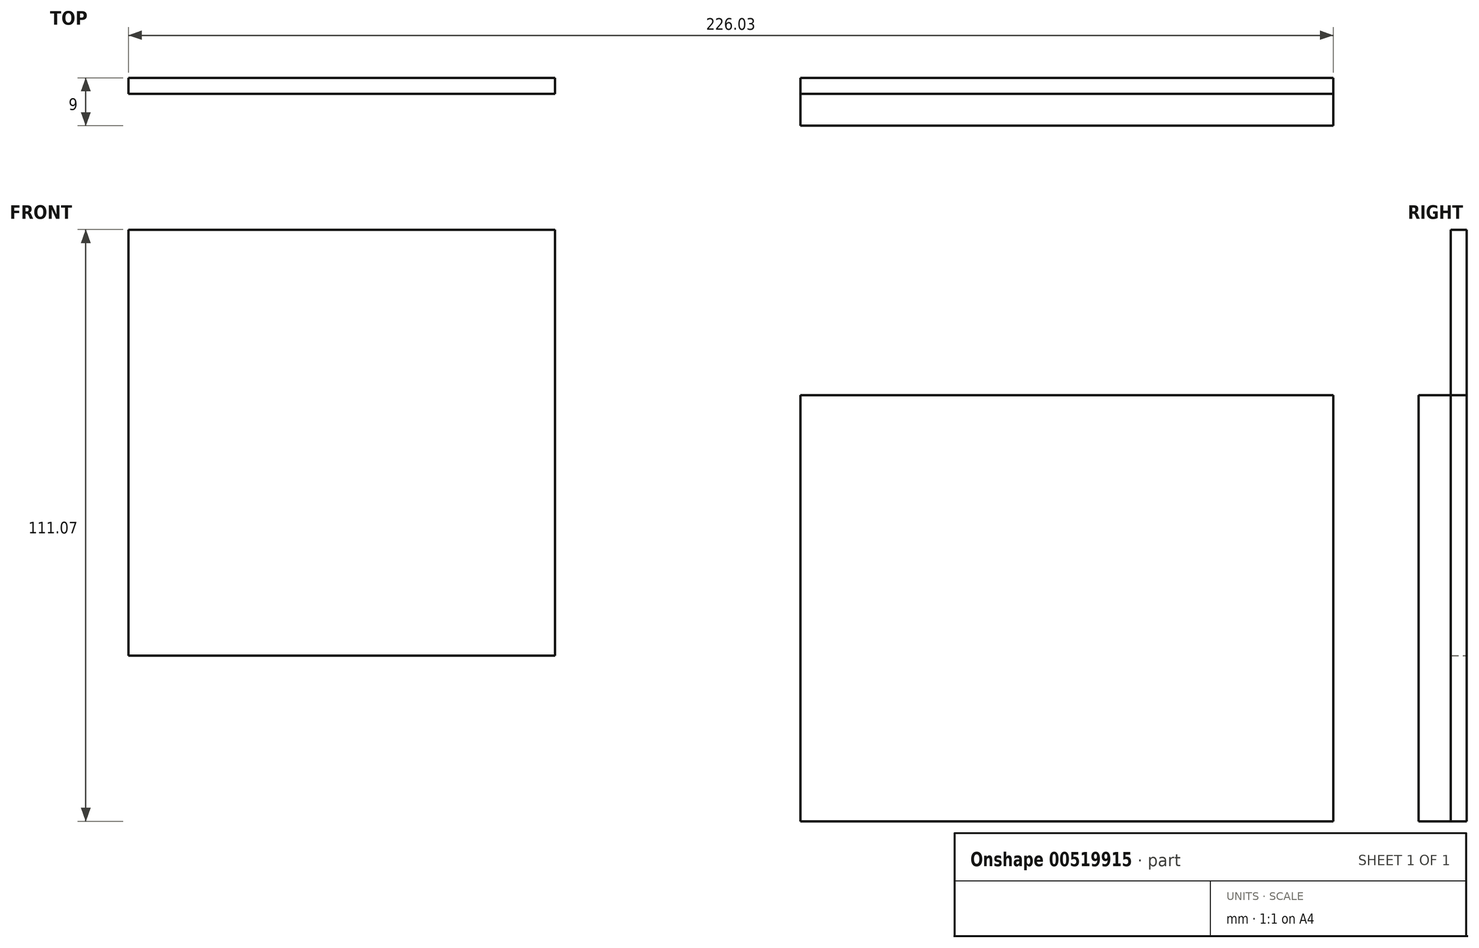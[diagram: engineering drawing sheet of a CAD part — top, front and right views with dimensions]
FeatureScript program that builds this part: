
annotation { "Feature Type Name" : "Feature", "Feature Type Description" : "" }
export const myFeature = defineFeature(function(context is Context, id is Id, definition is map)
    precondition{}
    {
        {
            var Q0;
            Q0=qCreatedBy(makeId("Front.planeOp"),FACE);
            var sketch = newSketch(context, id + "F0", { "sketchPlane" : qUnion([Q0])});
            skLineSegment(sketch, "E0.bottom", {"start": v(-116.27, 87.7) * mm, "end": v(-36.27, 87.7) * mm});
            skLineSegment(sketch, "E0.top", {"start": v(-116.27, 7.7) * mm, "end": v(-36.27, 7.7) * mm});
            skLineSegment(sketch, "E0.left", {"start": v(-116.27, 87.7) * mm, "end": v(-116.27, 7.7) * mm});
            skLineSegment(sketch, "E0.right", {"start": v(-36.27, 87.7) * mm, "end": v(-36.27, 7.7) * mm});
            skLineSegment(sketch, "E1.bottom", {"start": v(9.76, 56.64) * mm, "end": v(109.76, 56.64) * mm});
            skLineSegment(sketch, "E1.top", {"start": v(9.76, -23.36) * mm, "end": v(109.76, -23.36) * mm});
            skLineSegment(sketch, "E1.left", {"start": v(9.76, 56.64) * mm, "end": v(9.76, -23.36) * mm});
            skLineSegment(sketch, "E1.right", {"start": v(109.76, 56.64) * mm, "end": v(109.76, -23.36) * mm});
            skSolve(sketch);
        }
        {
            var Q0;
            Q0=makeQuery(id+"F0.imprint","IMPRINT",FACE,{"disambiguationData":[TD([[makeQuery(id+"F0.imprint","IMPRINT",EDGE,{"derivedFrom":sQuery(id+"F0.wireOp",EDGE,"E0.bottom")}),-1.0]])]});
            var Q1;
            Q1=makeQuery(id+"F0.imprint","IMPRINT",FACE,{"disambiguationData":[TD([[makeQuery(id+"F0.imprint","IMPRINT",EDGE,{"derivedFrom":sQuery(id+"F0.wireOp",EDGE,"E1.bottom")}),-1.0]])]});
            extrude(context, id + "F1", {"entities" : qUnion([Q0, Q1]), "depth" : 3 * mm, "offsetDistance" : 25 * mm});
        }
        {
            var Q0;
            Q0=makeQuery(id+"F1.opExtrude","CAP_FACE",FACE,{"disambiguationData":[OSD([sQuery(id+"F0.wireOp",EDGE,"E1.bottom"),sQuery(id+"F0.wireOp",EDGE,"E1.top"),sQuery(id+"F0.wireOp",EDGE,"E1.left"),sQuery(id+"F0.wireOp",EDGE,"E1.right")])],"isStart":false});
            extrude(context, id + "F2", {"entities" : qUnion([Q0]), "depth" : 6 * mm, "offsetDistance" : 25 * mm});
        }
    });
